# Revit family: Комби-клапан – регулятор расхода F_4006_HF_UHF
name_source: partatom
category: Rohrzubehör
revit_build: Autodesk Revit 2018 (Build: 20190510_1515(x64)
units: mm (PartAtom-declared; Revit-internal decimal feet)

## family parameters
Arbeitsebenenbasiert = Nein
Beim Laden mit Abzugskörper schneiden = Nein
Bemaßung runder Anschluss = Durchmesser verwenden
Gemeinsam genutzt = Nein
Immer vertikal = Ja
OmniClass-Nummer = 23.65.55.14
OmniClass-Titel = Valves for Liquid Services
Teiletyp = Unterbricht

## types (2) — shared parameters
D03 = 21 mm
D07 = 30 mm  [stored 0.0984252 ft]
D08 = 24 mm  [stored 0.0787402 ft]
D13 = 16 mm  [stored 0.0524934 ft]
D14 = 17 mm
D15 = 5 mm  [stored 0.0164042 ft]
D16 = 10 mm  [stored 0.0328084 ft]
D17 = 3 mm  [stored 0.00984252 ft]
D18 = 4 mm  [stored 0.0131234 ft]
H04 = 5 mm  [stored 0.0164042 ft]
H05 = 3 mm  [stored 0.00984252 ft]
H08 = 21 mm
H16 = 3 mm  [stored 0.00984252 ft]
H17 = 5 mm  [stored 0.0164042 ft]
H18 = 4 mm  [stored 0.0131234 ft]
Hersteller = Herz-Armaturen GmbH
K00 = 24 mm  [stored 0.0787402 ft]
K01 = 4 mm  [stored 0.0131234 ft]
K02 = 5 mm  [stored 0.0164042 ft]
K03 = 14 mm  [stored 0.0459318 ft]
L01 = 3 mm  [stored 0.00984252 ft]
L03 = 10 mm  [stored 0.0328084 ft]
M00 = 27 mm
M01 = 9 mm  [stored 0.0295276 ft]
M02 = 6 mm  [stored 0.019685 ft]
M03 = 3 mm  [stored 0.00984252 ft]
M04 = 2 mm  [stored 0.00656168 ft]
M05 = 4 mm  [stored 0.0131234 ft]
R02 = 13 mm
R03 = 7 mm  [stored 0.0229659 ft]
R04 = 8 mm  [stored 0.0262467 ft]
R05 = 5 mm  [stored 0.0164042 ft]
R97 = 2 mm  [stored 0.00656168 ft]
R98 = 6 mm  [stored 0.019685 ft]
R99 = 14 mm  [stored 0.0459318 ft]
SCRNCODE = 05;04;02
SCRNSEQ = ARM;ARM_TYP="DURR";2
URL = www.herz-armaturen.ru
Импульсная трубка = WN1.4301
Конус = CW617N-R320-S
Корпус = EN-GJL-250
Макс. рабочая температура = 110 °C
Максимальное рабочее давление = 1600000.0 Pa
Мембрана = EPDM
Мин. перепад давления = 400000.0 Pa
Мин. рабочая температура (с антифризом) = -20 °C
Мин. рабочая температура (чистая вода) = 2 °C
Область применения = Комби-клапан применяется в системах отопления и охлаждения с насосами. Комби-клапан автоматически ограничивает расход на выбранном участке системы до заданного значения, компенсируя все колебания давления. При этом нет необходимости в измерениях, а регулирование эффективно при любых условиях эксплуатации. Комби-клапан регулирует расход в соответствии с настройкой до заданного значения; на мембрану воздействует давление непосредственно до и после регулирующей части.
Перепад давления на oграничителе расхода = 20000.0 Pa
Седло = WN1.4305
Среда = Качество теплоносителя в соответствии с ÖNORM H5195 и/или предписаниями VDI-Standard 2035.
Разрешается использование смеси этилен- или пропиленгликоля в соотношении 25-50% с водой.
Уплотнения = EPDM
Фланцевое соединение = EN 1092-2
Шпиндель = WN1.4305

## per-type parameters (varying)
| type | HF | UHF |
| HF | Ja | Nein |
| UHF | Nein | Ja |

note: [stored X ft] marks values corroborated as IEEE doubles in the binary element streams (Revit-internal decimal feet)
